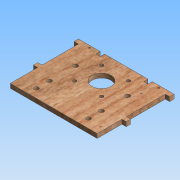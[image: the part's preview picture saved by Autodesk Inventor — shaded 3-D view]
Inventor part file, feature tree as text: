
AUTODESK INVENTOR PART (.ipt)
format: ipt  version: 2015 (Build 190159000, 159)  size: 297,984 bytes
history: native  units: mm
features: sketch x10, extrude x9, other x5, hole x3, projected_geometry x2, reference x2
ambient origin geometry x8: Origin, YZ Plane, XZ Plane, XY Plane, X Axis, Y Axis, Z Axis, Center Point
bodies: Body1 (feature_tree)
feature tree (31):
  other  "Blocks"
  extrude  "Extrusion2"  Depth=50.0mm
  hole  "Hole4"  [1 undecoded]
  hole  "Hole5"  [1 undecoded]
  hole  "Hole8"  [1 undecoded]
  extrude  "Extrusion11"  Depth=5.0mm
  extrude  "Extrusion12"  Depth=60.0mm
  extrude  "Extrusion13"  Depth=10.0mm
  sketch  "Sketch47"  dims[d78=22.0mm d79=6.0mm d80=4.0mm d81=2.0mm d82=90.0deg d83=2.0mm d84=0.0mm d176=30.0mm]
  extrude  "Extrusion14"  Depth=1.0mm
  extrude  "Extrusion15"  Depth=5.0mm
  extrude  "Extrusion16"  Depth=5.0mm TaperAngle=0.0deg
  extrude  "Extrusion17"  Depth=5.0mm TaperAngle=0.0deg
  extrude  "Extrusion18"  Depth=1.0mm
  sketch  "Sketch13"  dims[d21=100.0mm d22=50.0mm]
  sketch  "Sketch16"  dims[d23=5.0mm d24=0.0mm d43=31.0mm]
  sketch  "Sketch17"  dims[d44=31.0mm]
  other  "Block1"
  other  "Block2"
  other  "Block3"
  other  "Block4"
  projected_geometry  "Projected Loop3"
  sketch  "Sketch45"  dims[d45=4.0mm d46=6.0mm d47=4.0mm d48=2.0mm d49=90.0deg d50=4.0mm d51=0.0mm d52=60.0mm]
  projected_geometry  "Projected Loop4"
  reference  "Reference1"
  reference  "Reference2"
  sketch  "Sketch46"  dims[d53=5.2mm d54=6.0mm d55=4.0mm d56=2.0mm d57=90.0deg d58=4.0mm d59=0.0mm]
  sketch  "Sketch48"  dims[d179=5.0mm d184=5.0mm]
  sketch  "Sketch49"  dims[d185=10.0mm d189=60.0mm]
  sketch  "Sketch50"  dims[d190=30.0mm d191=10.0mm]
  sketch  "Sketch51"  dims[d192=5.0mm d193=15.0mm d196=5.0mm d197=5.0mm d198=0.0mm d200=5.0mm d201=0.0mm d202=47.0mm d203=5.0mm d204=5.0mm d205=20.0mm d206=5.0mm d207=5.0mm d208=20.0mm d209=10.0mm d210=0.0mm d211=2.0mm d212=2.5mm d213=10.0mm d214=2.0mm d215=10.0mm d216=2.5mm d217=10.0mm d218=0.0mm d219=10.0mm d220=0.0mm d221=5.0mm d222=5.0mm d223=5.0mm d224=5.0mm d225=5.0mm d226=0.0mm d227=5.0mm d228=5.0mm d229=45.0mm d230=5.0mm d231=0.0mm d232=5.0mm d233=5.0mm d234=45.0mm d235=5.0mm d236=0.0mm d29=1.0mm d30=1.0mm]
note: 3 required parameter values undecoded (feature->parameter linkage not recoverable at this tier; creation-order binding heuristic only, values carry confidence <= 0.55)
